# Revit family: Caroma Care 800 CF Invisi Suite
name_source: partatom
category: Plumbing Fixtures
revit_build: Autodesk Revit LT 2016 (Build: 20150220_1215(x64)
units: mm (PartAtom-declared; Revit-internal decimal feet)

## family parameters
Cut with Voids When Loaded = Yes
Host = Face
OmniClass Number = 23.45.05.21.11.11
OmniClass Title = Water Operated Water Closets
Part Type = Normal
Room Calculation Point = No
Round Connector Dimension = Use Diameter
Shared = No

## types (1)
- Standard
    Assembly Code = D2010110
    Backrest = Yes
    CW Connection = Yes
    CWFU = 1.18
    Default Elevation = 0 mm  [stored 0 ft]
    Description = Caroma Care 800 Wall Faced Invisi II Suite
    HW Connection = No
    Hardware = Metal-Stainless Steel-Brushed
    Height_ANZRS = 966 mm
    Keynote = WC
    Length_ANZRS = 800 mm
    Manufacturer = GWA Bathrooms & Kitchens
    Material_ANZRS = Porcelain-White-Caroma
    Model = 718200BW
    ModifiedIssue_ANZRS = 20140912 $
    No Backrest = No
    Seat = Porcelain-Sorrento Blue-Caroma
    Type Comments = White Only, S Trap Only, Sovereign 2000 Bottom Inlet Cistern, Trident Concealed Trap Care Pan, Raised Height Care Buttons
    URL = http://www.caroma.com.au
    Vent Connection = No
    WELSRating_ANZRS = WELS 4 Star rated, 4.5/3L
    WFU = 1.18
    Waste Connection = Yes
    WasteOutlet_ANZRS = 0
    Width_ANZRS = 350 mm  [stored 1.14829 ft]

note: [stored X ft] marks values corroborated as IEEE doubles in the binary element streams (Revit-internal decimal feet)

## geometry (parser evidence)
native form markers: Blend x8, Sweep x2
no freeform markers — native parametric forms only
